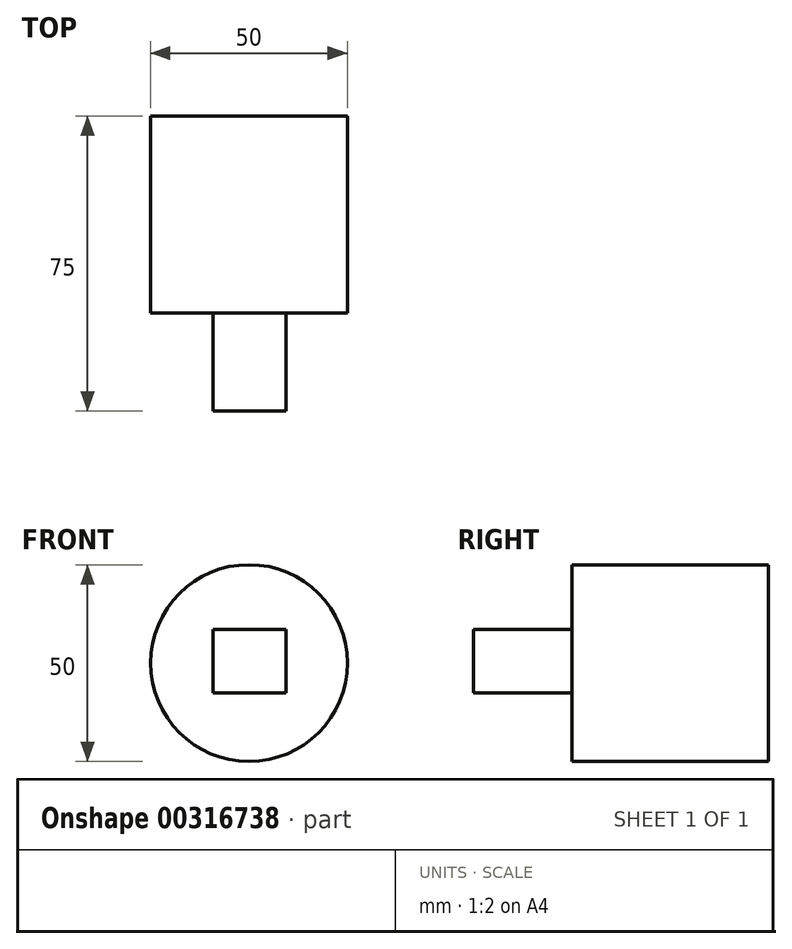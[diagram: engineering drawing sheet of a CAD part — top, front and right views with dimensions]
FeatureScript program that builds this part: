
annotation { "Feature Type Name" : "Feature", "Feature Type Description" : "" }
export const myFeature = defineFeature(function(context is Context, id is Id, definition is map)
    precondition{}
    {
        {
            var Q0;
            Q0=qCreatedBy(makeId("Front.planeOp"),FACE);
            var sketch = newSketch(context, id + "F0", { "sketchPlane" : qUnion([Q0])});
            skCircle(sketch, "E0", {"center": v(0, 0) * mm, "radius": 25 * mm});
            skSolve(sketch);
        }
        {
            var Q0;
            Q0 = qSketchRegion(id + "F0", true);
            extrude(context, id + "F1", {"entities" : qUnion([Q0]), "depth" : 50 * mm});
        }
        {
            var Q0;
            Q0=makeQuery(id+"F1.opExtrude","CAP_FACE",FACE,{"disambiguationData":[OSD([sQuery(id+"F0.wireOp",EDGE,"E0")])],"isStart":false});
            var sketch = newSketch(context, id + "F2", { "sketchPlane" : qUnion([Q0])});
            skLineSegment(sketch, "E1.bottom", {"start": v(-9.17, 8.5) * mm, "end": v(9.4, 8.5) * mm});
            skLineSegment(sketch, "E1.top", {"start": v(-9.17, -7.6) * mm, "end": v(9.4, -7.6) * mm});
            skLineSegment(sketch, "E1.left", {"start": v(-9.17, 8.5) * mm, "end": v(-9.17, -7.6) * mm});
            skLineSegment(sketch, "E1.right", {"start": v(9.4, 8.5) * mm, "end": v(9.4, -7.6) * mm});
            skSolve(sketch);
        }
        {
            var Q0;
            Q0 = qSketchRegion(id + "F2", true);
            extrude(context, id + "F3", {"entities" : qUnion([Q0]), "operationType" : NewBodyOperationType.ADD, "depth" : 25 * mm});
        }
    });
